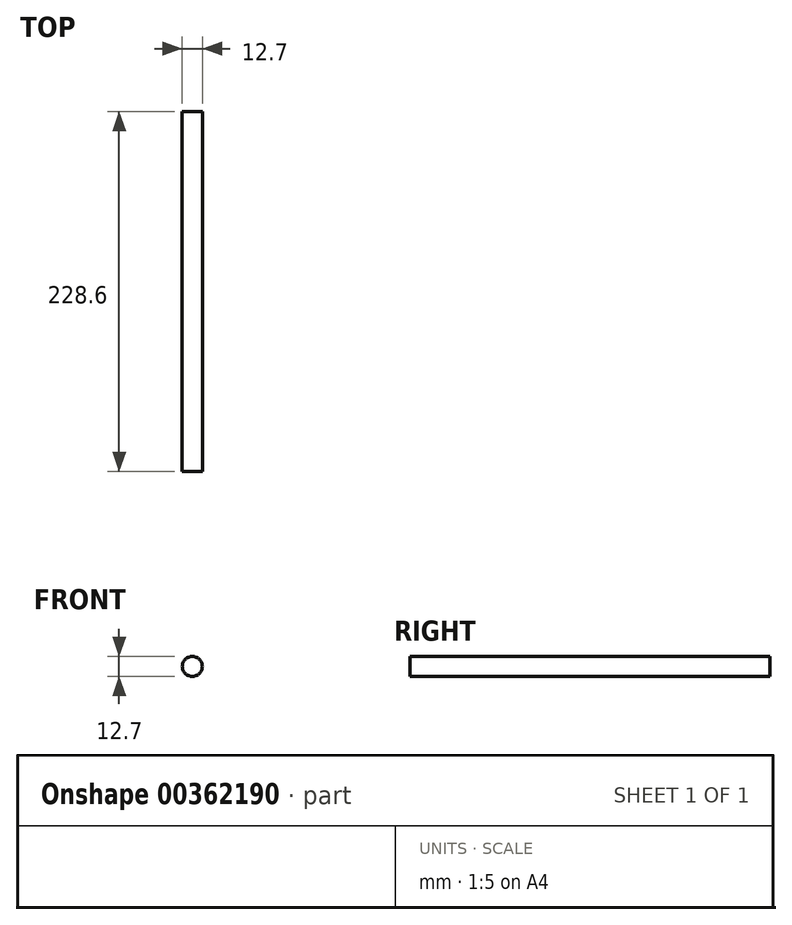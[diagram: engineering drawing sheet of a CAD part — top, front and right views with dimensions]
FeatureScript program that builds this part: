
annotation { "Feature Type Name" : "Feature", "Feature Type Description" : "" }
export const myFeature = defineFeature(function(context is Context, id is Id, definition is map)
    precondition{}
    {
        {
            var Q0;
            Q0=qCreatedBy(makeId("Front.planeOp"),FACE);
            var sketch = newSketch(context, id + "F0", { "sketchPlane" : qUnion([Q0])});
            skCircle(sketch, "E0", {"center": v(0, 0) * mm, "radius": 6.35 * mm});
            skSolve(sketch);
        }
        {
            var Q0;
            Q0=makeQuery(id+"F0.imprint","IMPRINT",FACE,{"disambiguationData":[TD([[makeQuery(id+"F0.imprint","IMPRINT",EDGE,{"derivedFrom":sQuery(id+"F0.wireOp",EDGE,"E0")}),1.0]])]});
            extrude(context, id + "F1", {"entities" : qUnion([Q0]), "depth" : 228.6 * mm});
        }
    });
